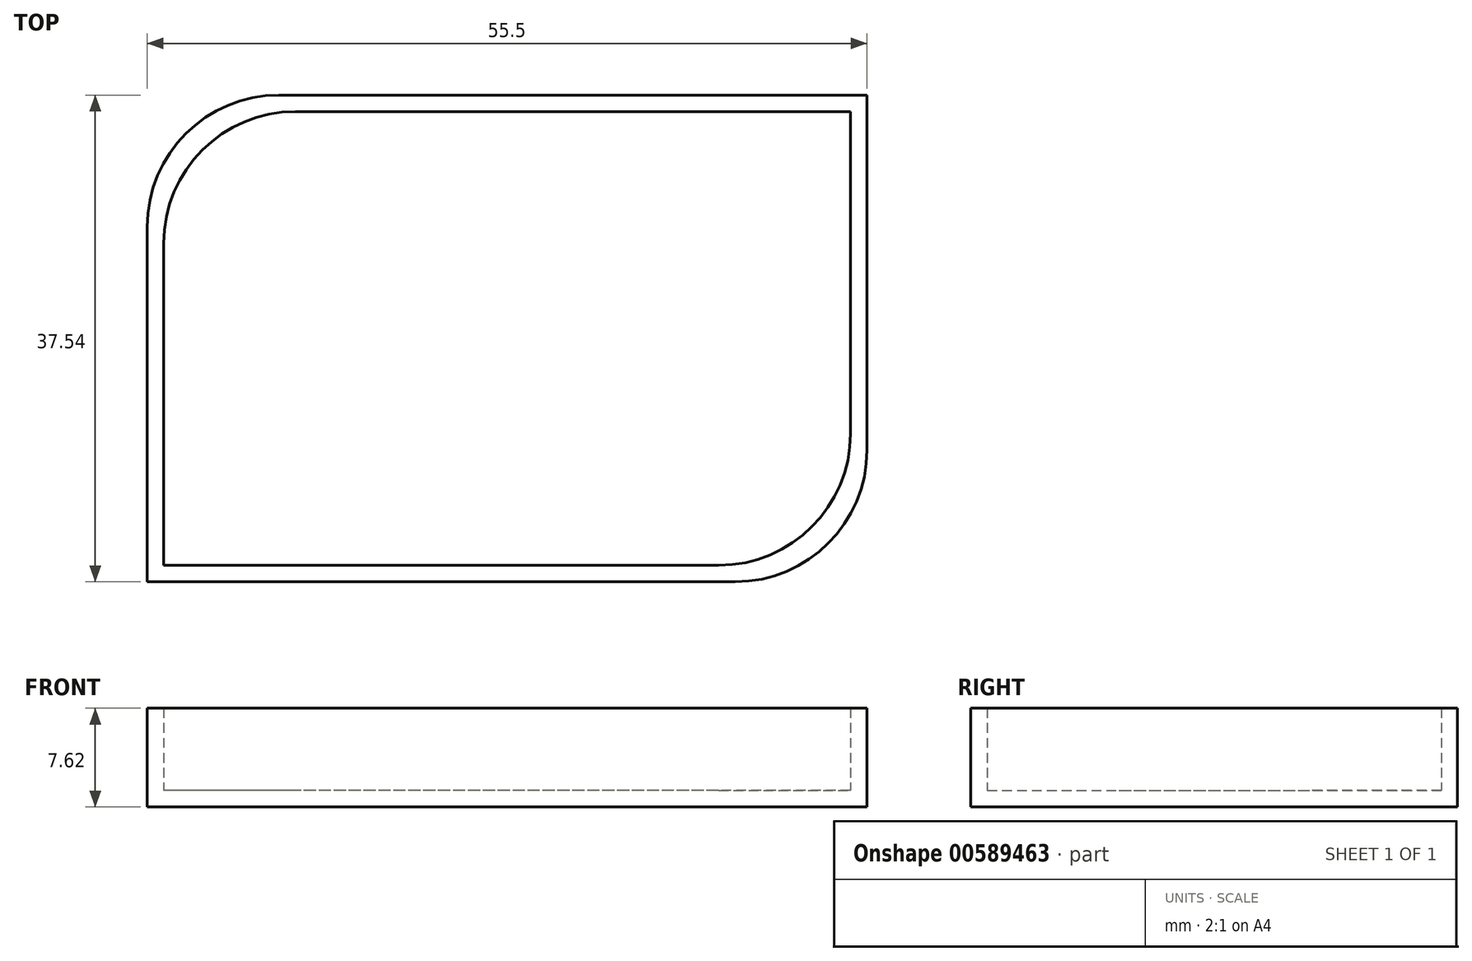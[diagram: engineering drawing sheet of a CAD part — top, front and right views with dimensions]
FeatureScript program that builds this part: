
annotation { "Feature Type Name" : "Feature", "Feature Type Description" : "" }
export const myFeature = defineFeature(function(context is Context, id is Id, definition is map)
    precondition{}
    {
        {
            var Q0;
            Q0=qCreatedBy(makeId("Top.planeOp"),FACE);
            var sketch = newSketch(context, id + "F0", { "sketchPlane" : qUnion([Q0])});
            skLineSegment(sketch, "E0.bottom", {"start": v(-64.95, 22.74) * mm, "end": v(-9.45, 22.74) * mm});
            skLineSegment(sketch, "E0.top", {"start": v(-64.95, -14.8) * mm, "end": v(-9.45, -14.8) * mm});
            skLineSegment(sketch, "E0.left", {"start": v(-64.95, 22.74) * mm, "end": v(-64.95, -14.8) * mm});
            skLineSegment(sketch, "E0.right", {"start": v(-9.45, 22.74) * mm, "end": v(-9.45, -14.8) * mm});
            skLineSegment(sketch, "E1.bottom", {"start": v(-63.68, 21.47) * mm, "end": v(-10.72, 21.47) * mm});
            skLineSegment(sketch, "E1.top", {"start": v(-63.68, -13.53) * mm, "end": v(-10.72, -13.53) * mm});
            skLineSegment(sketch, "E1.left", {"start": v(-63.68, 21.47) * mm, "end": v(-63.68, -13.53) * mm});
            skLineSegment(sketch, "E1.right", {"start": v(-10.72, 21.47) * mm, "end": v(-10.72, -13.53) * mm});
            skSolve(sketch);
        }
        {
            var Q0;
            Q0 = qSketchRegion(id + "F0", true);
            var Q1;
            Q1=makeQuery(id+"F0.imprint","IMPRINT",FACE,{"disambiguationData":[TD([[makeQuery(id+"F0.imprint","IMPRINT",EDGE,{"derivedFrom":sQuery(id+"F0.wireOp",EDGE,"E1.bottom")}),-1.0]])]});
            extrude(context, id + "F1", {"entities" : qUnion([Q0, Q1]), "depth" : 1.27 * mm, "offsetDistance" : 25.4 * mm});
        }
        {
            var Q0;
            Q0 = qSketchRegion(id + "F0", true);
            extrude(context, id + "F2", {"entities" : qUnion([Q0]), "operationType" : NewBodyOperationType.ADD, "depth" : 7.62 * mm, "offsetDistance" : 25.4 * mm});
        }
        {
            var Q0;
            {var subQ0=sQuery(id+"F0.wireOp",EDGE,"E0.left");var subQ1=sQuery(id+"F0.wireOp",EDGE,"E0.bottom");Q0=makeQuery(id+"F2.boolean.opBoolean","MERGE",EDGE,{"derivedFrom":[makeQuery(id+"F1.opExtrude","SWEPT_EDGE",EDGE,{"disambiguationData":[OSD([subQ1,subQ0])]}),makeQuery(id+"F2.opExtrude","SWEPT_EDGE",EDGE,{"disambiguationData":[OSD([subQ1,subQ0])]})]});}
            var Q1;
            Q1=makeQuery(id+"F2.opExtrude","SWEPT_EDGE",EDGE,{"disambiguationData":[OSD([sQuery(id+"F0.wireOp",EDGE,"E1.bottom"),sQuery(id+"F0.wireOp",EDGE,"E1.left")])]});
            var Q2;
            Q2=makeQuery(id+"F2.opExtrude","SWEPT_EDGE",EDGE,{"disambiguationData":[OSD([sQuery(id+"F0.wireOp",EDGE,"E1.top"),sQuery(id+"F0.wireOp",EDGE,"E1.right")])]});
            var Q3;
            {var subQ0=sQuery(id+"F0.wireOp",EDGE,"E0.right");var subQ1=sQuery(id+"F0.wireOp",EDGE,"E0.top");Q3=makeQuery(id+"F2.boolean.opBoolean","MERGE",EDGE,{"derivedFrom":[makeQuery(id+"F1.opExtrude","SWEPT_EDGE",EDGE,{"disambiguationData":[OSD([subQ1,subQ0])]}),makeQuery(id+"F2.opExtrude","SWEPT_EDGE",EDGE,{"disambiguationData":[OSD([subQ1,subQ0])]})]});}
            fillet(context, id + "F3", {"entities" : qUnion([Q0, Q1, Q2, Q3]), "radius" : 10.16 * mm, "tangentPropagation" : true, "allowEdgeOverflow" : false});
        }
    });
